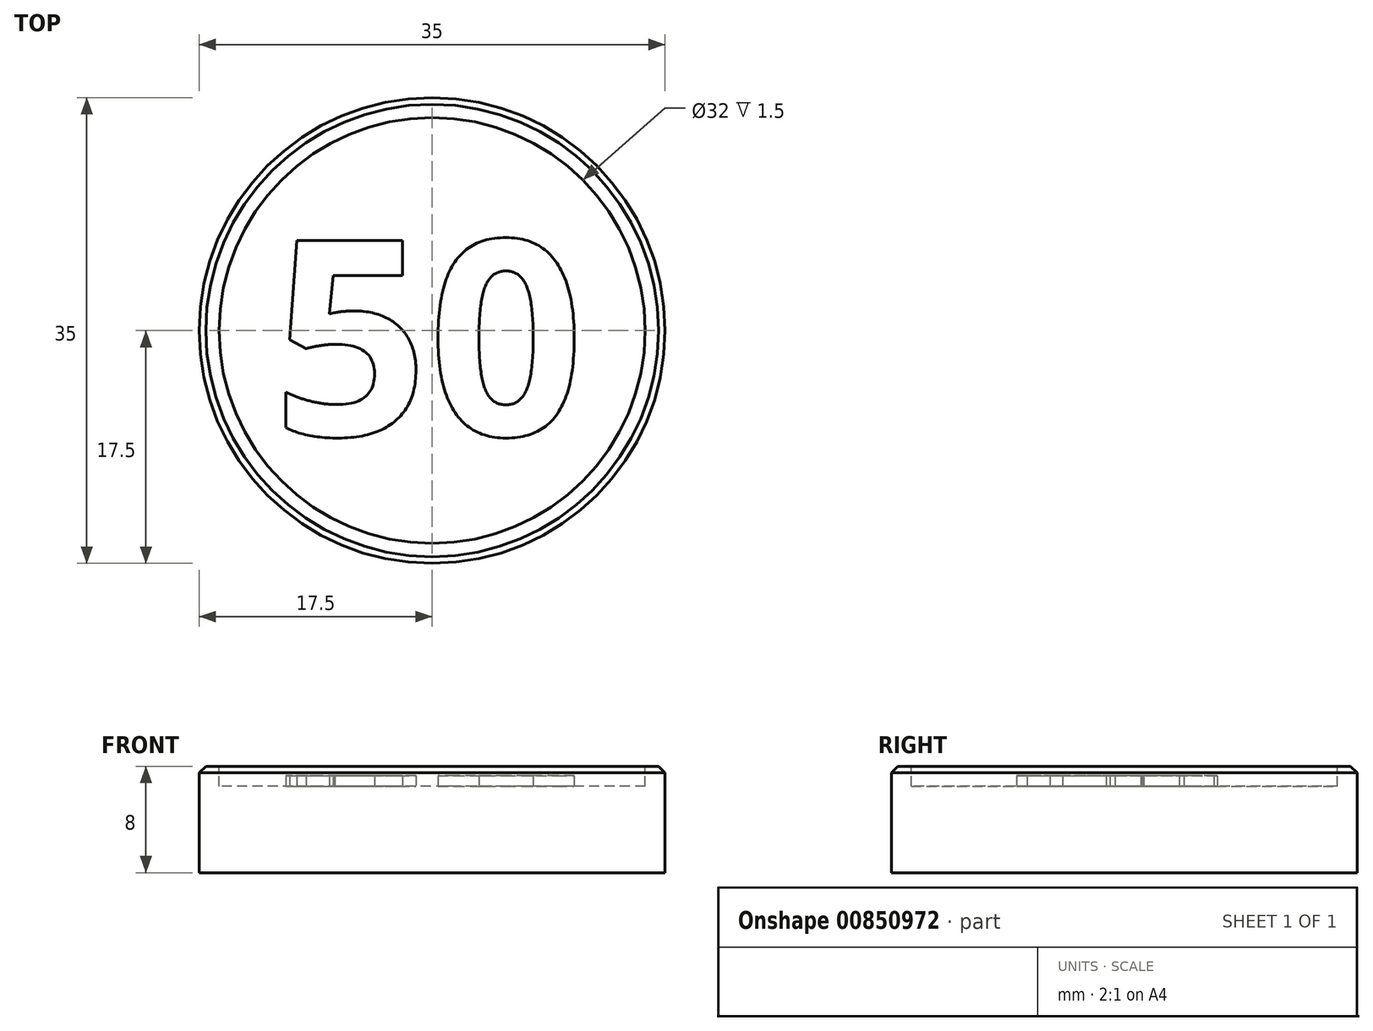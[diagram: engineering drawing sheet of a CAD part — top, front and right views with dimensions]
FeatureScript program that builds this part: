
annotation { "Feature Type Name" : "Feature", "Feature Type Description" : "" }
export const myFeature = defineFeature(function(context is Context, id is Id, definition is map)
    precondition{}
    {
        {
            var Q0;
            Q0=qCreatedBy(makeId("Top.planeOp"),FACE);
            var sketch = newSketch(context, id + "F0", { "sketchPlane" : qUnion([Q0])});
            skCircle(sketch, "E0", {"center": v(0, 0) * mm, "radius": 17.5 * mm});
            skSolve(sketch);
        }
        {
            var Q0;
            Q0 = qSketchRegion(id + "F0", true);
            extrude(context, id + "F1", {"entities" : qUnion([Q0]), "depth" : 8 * mm, "offsetDistance" : 25 * mm});
        }
        {
            var Q0;
            Q0=makeQuery(id+"F1.opExtrude","CAP_FACE",FACE,{"disambiguationData":[OSD([sQuery(id+"F0.wireOp",EDGE,"E0")])],"isStart":false});
            var sketch = newSketch(context, id + "F2", { "sketchPlane" : qUnion([Q0])});
            skPoint(sketch, "E1.first.point", {"position": v(-10.59, -13.93) * mm});
            skPoint(sketch, "E1.second.point", {"position": v(17.5, 0) * mm});
            skPoint(sketch, "E1.third.point", {"position": v(-5.38, 16.65) * mm});
            skCircle(sketch, "E2", {"center": v(0, 0) * mm, "radius": 16 * mm});
            skSolve(sketch);
        }
        {
            var Q0;
            Q0 = qSketchRegion(id + "F2", true);
            extrude(context, id + "F3", {"entities" : qUnion([Q0]), "operationType" : NewBodyOperationType.REMOVE, "oppositeDirection" : true, "depth" : 1.5 * mm, "offsetDistance" : 25 * mm});
        }
        {
            var Q0;
            Q0=makeQuery(id+"F1.opExtrude","CAP_EDGE",EDGE,{"disambiguationData":[OSD([sQuery(id+"F0.wireOp",EDGE,"E0")])],"isStart":false});
            chamfer(context, id + "F4", {"entities" : qUnion([Q0]), "width" : 0.5 * mm, "tangentPropagation" : true});
        }
        {
            var Q0;
            Q0=makeQuery(id+"F3.boolean.opBoolean","COPY",FACE,{"derivedFrom":makeQuery(id+"F3.opExtrude","CAP_FACE",FACE,{"disambiguationData":[OSD([sQuery(id+"F2.wireOp",EDGE,"E2")])],"isStart":false})});
            var sketch = newSketch(context, id + "F5", { "sketchPlane" : qUnion([Q0])});
            skText(sketch, "E3", { "text": "50", "fontName": "OpenSans-Bold.ttf"});
            const initialGuessF5  = {"E3": [-0.012, -0.00788, 1, 0, 0.01476]};
            skSetInitialGuess(sketch, initialGuessF5);
            skSolve(sketch);
        }
        {
            var Q0;
            Q0 = qSketchRegion(id + "F5", true);
            extrude(context, id + "F6", {"entities" : qUnion([Q0]), "operationType" : NewBodyOperationType.ADD, "depth" : 0.8 * mm, "offsetDistance" : 25 * mm});
        }
    });
